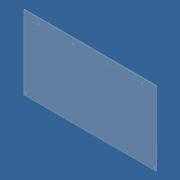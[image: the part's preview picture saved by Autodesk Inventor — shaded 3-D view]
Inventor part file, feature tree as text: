
AUTODESK INVENTOR PART (.ipt)
format: ipt  version: 2012 (Build 160160000, 160)  size: 81,920 bytes
history: native  units: in
note: dims shown in document units (in); Inventor stores cm internally (conversion verified against a paired STEP export)
features: hole x2, pattern_linear x2, extrude x1, sketch x1
ambient origin geometry x8: Origin, YZ Plane, XZ Plane, XY Plane, X Axis, Y Axis, Z Axis, Center Point
bodies: Solid1 (feature_tree)
feature tree (6):
  extrude  "Extrusion1"  Depth=28.0in
  hole  "Hole1"  [1 undecoded]
  pattern_linear  "Rectangular Pattern1"  Count1=4 Spacing1=13.0in
  hole  "Hole2"  [1 undecoded]
  pattern_linear  "Rectangular Pattern2"  [2 undecoded]
  sketch  "Sketch1"  dims[d0=50.0in d1=28.0in d7=0.25in d8=0.0in d9=5.5in d10=2.0in d11=0.5in d12=0.75in d13=0.375in d14=0.25in d15=0.5635in d16=1.0in d17=0.8108in d18=1.5748in d20=13.0in d21=0.75in d22=1.0in d23=0.5in d24=0.75in d25=0.375in d26=0.25in d27=0.5635in d28=1.0in d29=0.8108in d30=0.7874in d32=48.5in]
note: 4 required parameter values undecoded (feature->parameter linkage not recoverable at this tier; creation-order binding heuristic only, values carry confidence <= 0.55)
